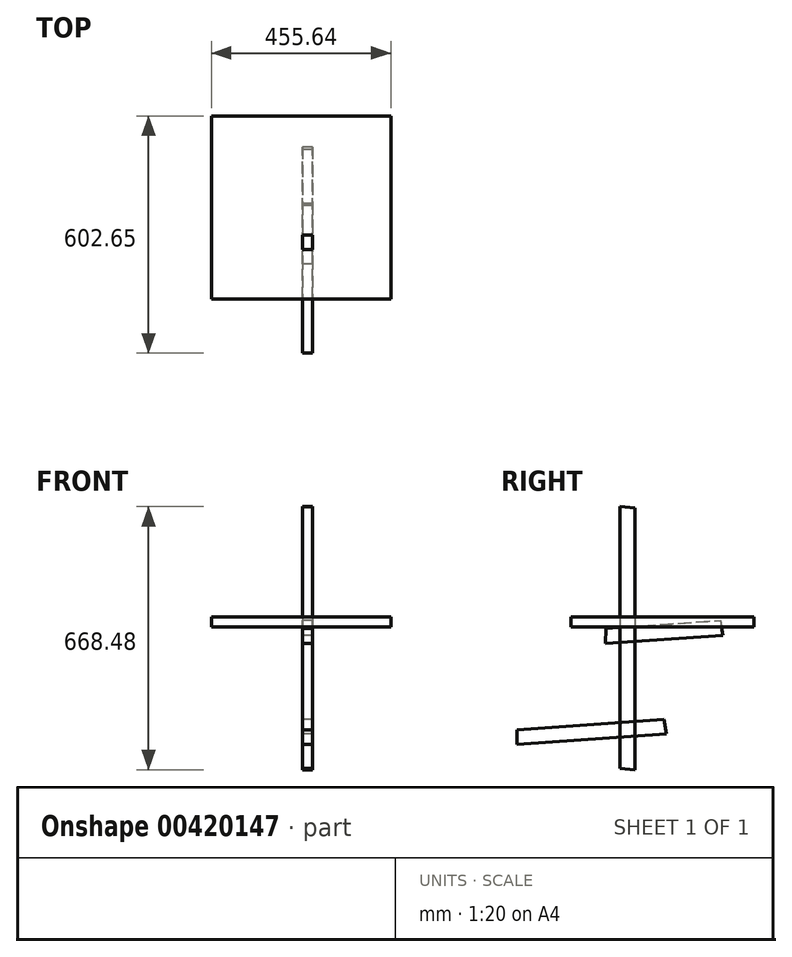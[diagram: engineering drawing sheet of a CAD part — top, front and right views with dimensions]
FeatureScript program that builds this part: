
annotation { "Feature Type Name" : "Feature", "Feature Type Description" : "" }
export const myFeature = defineFeature(function(context is Context, id is Id, definition is map)
    precondition{}
    {
        {
            var Q0;
            Q0=qCreatedBy(makeId("Right.planeOp"),FACE);
            var sketch = newSketch(context, id + "F0", { "sketchPlane" : qUnion([Q0])});
            skLineSegment(sketch, "E0.left", {"start": v(-109.87, 306.07) * mm, "end": v(-109.87, -359.1) * mm});
            skLineSegment(sketch, "E0.right", {"start": v(-71.91, 302.75) * mm, "end": v(-71.91, -362.41) * mm});
            skLineSegment(sketch, "E1", {"start": v(-109.87, -359.1) * mm, "end": v(-71.91, -362.41) * mm});
            skLineSegment(sketch, "E2", {"start": v(-71.91, -362.41) * mm, "end": v(-159.69, -362.41) * mm, "construction": true});
            skLineSegment(sketch, "E3", {"start": v(-71.91, 256.13) * mm, "end": v(-71.91, 302.75) * mm});
            skPoint(sketch, "E4.end.orphan", {"position": v(-71.91, 279.44) * mm});
            skPoint(sketch, "E4.start.orphan", {"position": v(390.1, 283) * mm});
            skPoint(sketch, "E5.orphan", {"position": v(390.1, 254.66) * mm});
            skPoint(sketch, "E6.start.orphan", {"position": v(390.1, 311.33) * mm});
            skLineSegment(sketch, "E7", {"start": v(-335.5, 299.26) * mm, "end": v(-335.5, 299.25) * mm});
            skLineSegment(sketch, "E8", {"start": v(-109.87, 306.07) * mm, "end": v(-71.91, 302.75) * mm});
            skLineSegment(sketch, "E9", {"start": v(-71.91, 302.75) * mm, "end": v(-109.87, 306.07) * mm});
            skLineSegment(sketch, "E10", {"start": v(-109.1, 302.75) * mm, "end": v(-71.91, 302.75) * mm});
            skSolve(sketch);
        }
        {
            var Q0;
            Q0 = qSketchRegion(id + "F0", true);
            extrude(context, id + "F1", {"entities" : qUnion([Q0]), "depth" : 25.4 * mm});
        }
        {
            var Q0;
            Q0=qCreatedBy(makeId("Top.planeOp"),FACE);
            var sketch = newSketch(context, id + "F2", { "sketchPlane" : qUnion([Q0])});
            skLineSegment(sketch, "E11.bottom", {"start": v(-231.58, 230.4) * mm, "end": v(224.06, 230.4) * mm});
            skLineSegment(sketch, "E11.top", {"start": v(-231.58, -234.52) * mm, "end": v(224.06, -234.52) * mm});
            skLineSegment(sketch, "E11.left", {"start": v(-231.58, 230.4) * mm, "end": v(-231.58, -234.52) * mm});
            skLineSegment(sketch, "E11.right", {"start": v(224.06, 230.4) * mm, "end": v(224.06, -234.52) * mm});
            skSolve(sketch);
        }
        {
            var Q0;
            Q0 = qSketchRegion(id + "F2", true);
            extrude(context, id + "F3", {"entities" : qUnion([Q0]), "depth" : 25.4 * mm});
        }
        {
            var Q0;
            Q0=makeQuery(id+"F0.imprint","IMPRINT",FACE,{"disambiguationData":[TD([[makeQuery(id+"F0.imprint","IMPRINT",EDGE,{"derivedFrom":sQuery(id+"F0.wireOp",EDGE,"E0.left")}),1.0]])]});
            var sketch = newSketch(context, id + "F4", { "sketchPlane" : qUnion([Q0])});
            skLineSegment(sketch, "E12", {"start": v(2.13, -235.36) * mm, "end": v(7.82, -271.34) * mm});
            skLineSegment(sketch, "E13", {"start": v(7.82, -271.34) * mm, "end": v(-372.25, -297.85) * mm});
            skLineSegment(sketch, "E14", {"start": v(-372.25, -297.85) * mm, "end": v(-371.61, -261.43) * mm});
            skLineSegment(sketch, "E15", {"start": v(-371.61, -261.43) * mm, "end": v(2.13, -235.36) * mm});
            skLineSegment(sketch, "E16", {"start": v(-372.25, -297.85) * mm, "end": v(-376.58, -235.88) * mm, "construction": true});
            skLineSegment(sketch, "E17", {"start": v(7.82, -271.34) * mm, "end": v(3.27, -206.02) * mm, "construction": true});
            skSolve(sketch);
        }
        {
            var Q0;
            Q0 = qSketchRegion(id + "F4", true);
            extrude(context, id + "F5", {"entities" : qUnion([Q0]), "depth" : 25.4 * mm});
        }
        {
            var Q0;
            Q0=qCreatedBy(makeId("Right.planeOp"),FACE);
            var sketch = newSketch(context, id + "F6", { "sketchPlane" : qUnion([Q0])});
            skLineSegment(sketch, "E18", {"start": v(145.1, 16.78) * mm, "end": v(151.07, -21) * mm});
            skLineSegment(sketch, "E19", {"start": v(151.07, -21) * mm, "end": v(-146.66, -41.77) * mm});
            skLineSegment(sketch, "E20", {"start": v(-146.66, -41.77) * mm, "end": v(-145.99, -3.53) * mm});
            skLineSegment(sketch, "E21", {"start": v(-145.99, -3.53) * mm, "end": v(145.1, 16.78) * mm});
            skLineSegment(sketch, "E22", {"start": v(-146.66, -41.77) * mm, "end": v(-152.12, 36.52) * mm, "construction": true});
            skLineSegment(sketch, "E23", {"start": v(151.07, -21) * mm, "end": v(145.43, 59.81) * mm, "construction": true});
            skSolve(sketch);
        }
        {
            var Q0;
            Q0 = qSketchRegion(id + "F6", true);
            extrude(context, id + "F7", {"entities" : qUnion([Q0]), "depth" : 25.4 * mm});
        }
    });
